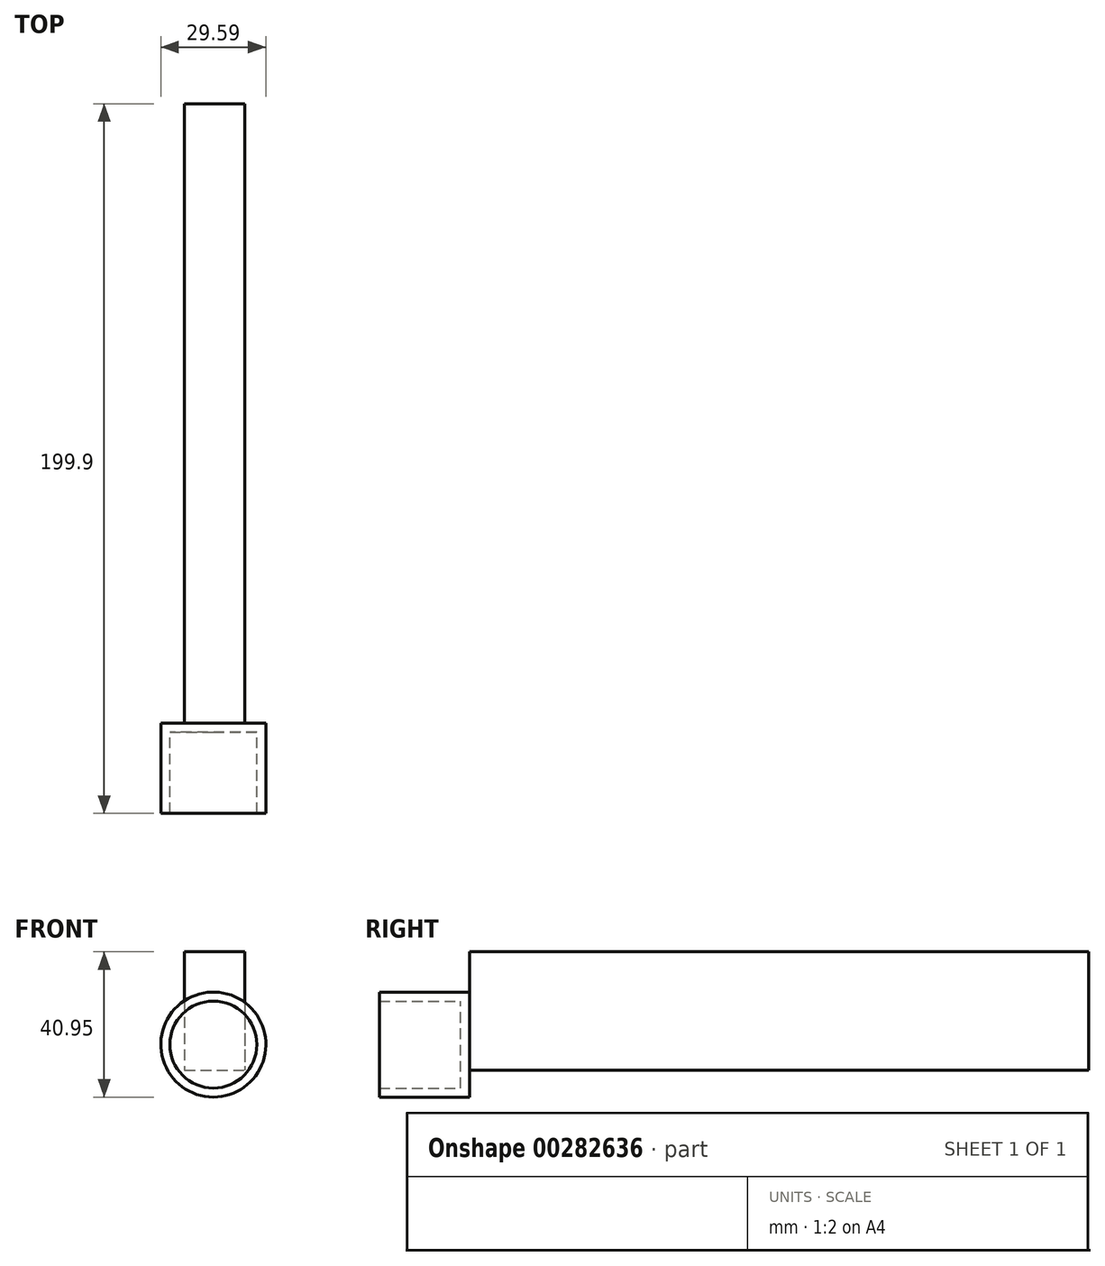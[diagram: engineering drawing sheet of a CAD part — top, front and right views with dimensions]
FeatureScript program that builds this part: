
annotation { "Feature Type Name" : "Feature", "Feature Type Description" : "" }
export const myFeature = defineFeature(function(context is Context, id is Id, definition is map)
    precondition{}
    {
        {
            var Q0;
            Q0=qCreatedBy(makeId("Front.planeOp"),FACE);
            var sketch = newSketch(context, id + "F0", { "sketchPlane" : qUnion([Q0])});
            skCircle(sketch, "E0", {"center": v(-10, 5.22) * mm, "radius": 14.8 * mm});
            skSolve(sketch);
        }
        {
            var Q0;
            Q0=makeQuery(id+"F0.imprint","IMPRINT",FACE,{"disambiguationData":[TD([[makeQuery(id+"F0.imprint","IMPRINT",EDGE,{"derivedFrom":sQuery(id+"F0.wireOp",EDGE,"E0")}),1.0]])]});
            extrude(context, id + "F1", {"entities" : qUnion([Q0]), "depth" : 25.4 * mm});
        }
        {
            var Q0;
            Q0=makeQuery(id+"F1.opExtrude","CAP_FACE",FACE,{"disambiguationData":[OSD([sQuery(id+"F0.wireOp",EDGE,"E0")])],"isStart":false});
            shell(context, id + "F2", {"entities" : qUnion([Q0]), "thickness" : 2.54 * mm});
        }
        {
            var Q0;
            Q0=qCreatedBy(makeId("Front.planeOp"),FACE);
            var sketch = newSketch(context, id + "F3", { "sketchPlane" : qUnion([Q0])});
            skLineSegment(sketch, "E1.bottom", {"start": v(-18.17, 31.37) * mm, "end": v(-1.1, 31.37) * mm});
            skLineSegment(sketch, "E1.top", {"start": v(-18.17, -2) * mm, "end": v(-1.1, -2) * mm});
            skLineSegment(sketch, "E1.left", {"start": v(-18.17, 31.37) * mm, "end": v(-18.17, -2) * mm});
            skLineSegment(sketch, "E1.right", {"start": v(-1.1, 31.37) * mm, "end": v(-1.1, -2) * mm});
            skPoint(sketch, "E1.middle", {"position": v(-9.64, 14.68) * mm});
            skSolve(sketch);
        }
        {
            var Q0;
            Q0=makeQuery(id+"F3.imprint","IMPRINT",FACE,{"disambiguationData":[TD([[makeQuery(id+"F3.imprint","IMPRINT",EDGE,{"derivedFrom":sQuery(id+"F3.wireOp",EDGE,"E1.bottom")}),-1.0]])]});
            extrude(context, id + "F4", {"entities" : qUnion([Q0]), "operationType" : NewBodyOperationType.ADD, "oppositeDirection" : true, "depth" : 174.5 * mm});
        }
    });
